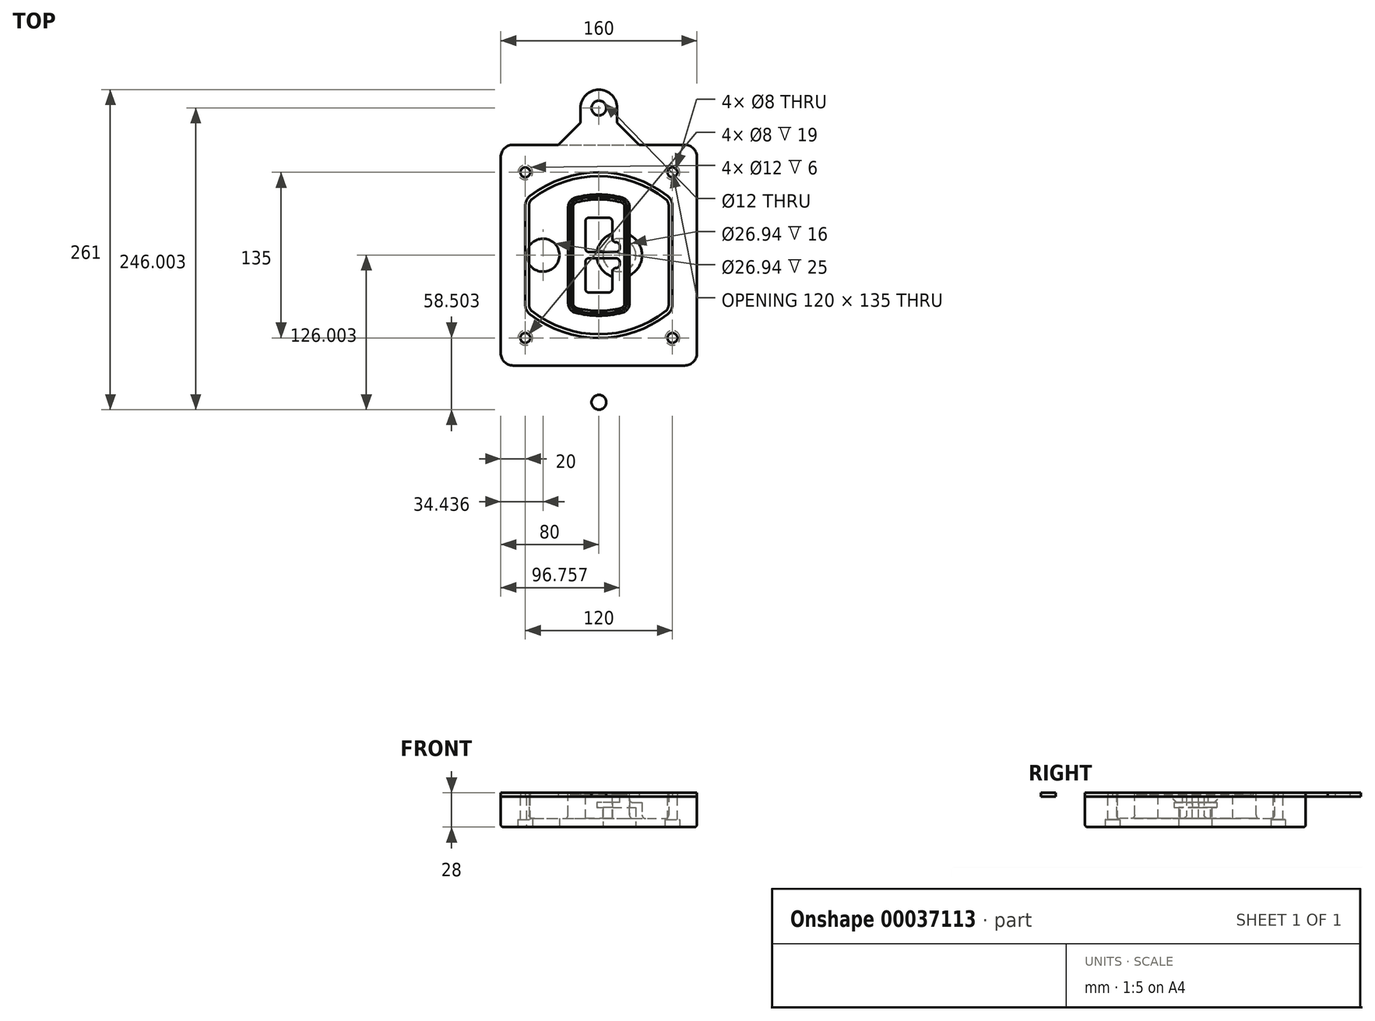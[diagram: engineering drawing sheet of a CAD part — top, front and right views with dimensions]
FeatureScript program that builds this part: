
annotation { "Feature Type Name" : "Feature", "Feature Type Description" : "" }
export const myFeature = defineFeature(function(context is Context, id is Id, definition is map)
    precondition{}
    {
        {
            var Q0;
            Q0=qCreatedBy(makeId("Top.planeOp"),FACE);
            var sketch = newSketch(context, id + "F0", { "sketchPlane" : qUnion([Q0])});
            skPoint(sketch, "E0.rect.middle", {"position": v(0, 0) * mm});
            skLineSegment(sketch, "E1.bottom", {"start": v(24.05, 28.38) * mm, "end": v(164.05, 28.38) * mm});
            skLineSegment(sketch, "E1.top", {"start": v(24.05, 208.38) * mm, "end": v(164.05, 208.38) * mm});
            skLineSegment(sketch, "E1.left", {"start": v(14.05, 38.38) * mm, "end": v(14.05, 198.38) * mm});
            skLineSegment(sketch, "E1.right", {"start": v(174.05, 38.38) * mm, "end": v(174.05, 198.38) * mm});
            skLineSegment(sketch, "E2", {"start": v(14.05, 208.38) * mm, "end": v(174.05, 28.38) * mm, "construction": true});
            skLineSegment(sketch, "E3", {"start": v(174.05, 208.38) * mm, "end": v(14.05, 28.38) * mm, "construction": true});
            skCircle(sketch, "E4", {"center": v(34.05, 185.88) * mm, "radius": 4 * mm});
            skCircle(sketch, "E5", {"center": v(154.05, 185.88) * mm, "radius": 4 * mm});
            skCircle(sketch, "E6", {"center": v(154.05, 50.88) * mm, "radius": 4 * mm});
            skCircle(sketch, "E7", {"center": v(34.05, 50.88) * mm, "radius": 4 * mm});
            skLineSegment(sketch, "E8", {"start": v(34.05, 185.88) * mm, "end": v(154.05, 185.88) * mm, "construction": true});
            skLineSegment(sketch, "E9", {"start": v(154.05, 185.88) * mm, "end": v(154.05, 50.88) * mm, "construction": true});
            skLineSegment(sketch, "E10", {"start": v(154.05, 50.88) * mm, "end": v(34.05, 50.88) * mm, "construction": true});
            skLineSegment(sketch, "E11", {"start": v(34.05, 50.88) * mm, "end": v(34.05, 185.88) * mm, "construction": true});
            skLineSegment(sketch, "E12", {"start": v(34.05, 158.68) * mm, "end": v(34.05, 78.09) * mm});
            skLineSegment(sketch, "E13", {"start": v(154.05, 158.68) * mm, "end": v(154.05, 78.09) * mm});
            skArc(sketch, "E14", {"start": v(150.2, 166.56) * mm, "mid": v(94.05, 185.88) * mm, "end": v(37.9, 166.56) * mm});
            skArc(sketch, "E15", {"start": v(37.9, 70.2) * mm, "mid": v(94.05, 50.88) * mm, "end": v(150.2, 70.2) * mm});
            skLineSegment(sketch, "E16", {"start": v(34.05, 118.38) * mm, "end": v(154.05, 118.38) * mm, "construction": true});
            skPoint(sketch, "E17.visualSharp", {"position": v(34.05, 73.38) * mm});
            skArc(sketch, "E17.filletArc", {"start": v(34.05, 78.09) * mm, "mid": v(35.06, 73.7) * mm, "end": v(37.9, 70.2) * mm});
            skPoint(sketch, "E18.visualSharp", {"position": v(34.05, 163.38) * mm});
            skArc(sketch, "E18.filletArc", {"start": v(37.9, 166.56) * mm, "mid": v(35.06, 163.06) * mm, "end": v(34.05, 158.68) * mm});
            skPoint(sketch, "E19.visualSharp", {"position": v(154.05, 163.38) * mm});
            skArc(sketch, "E19.filletArc", {"start": v(154.05, 158.68) * mm, "mid": v(153.04, 163.06) * mm, "end": v(150.2, 166.56) * mm});
            skPoint(sketch, "E20.visualSharp", {"position": v(154.05, 73.38) * mm});
            skArc(sketch, "E20.filletArc", {"start": v(150.2, 70.2) * mm, "mid": v(153.04, 73.7) * mm, "end": v(154.05, 78.09) * mm});
            skPoint(sketch, "E21.visualSharp", {"position": v(14.05, 208.38) * mm});
            skArc(sketch, "E21.filletArc", {"start": v(24.05, 208.38) * mm, "mid": v(16.98, 205.45) * mm, "end": v(14.05, 198.38) * mm});
            skPoint(sketch, "E22.visualSharp", {"position": v(174.05, 208.38) * mm});
            skArc(sketch, "E22.filletArc", {"start": v(174.05, 198.38) * mm, "mid": v(171.12, 205.45) * mm, "end": v(164.05, 208.38) * mm});
            skPoint(sketch, "E23.visualSharp", {"position": v(174.05, 28.38) * mm});
            skArc(sketch, "E23.filletArc", {"start": v(164.05, 28.38) * mm, "mid": v(171.12, 31.31) * mm, "end": v(174.05, 38.38) * mm});
            skPoint(sketch, "E24.visualSharp", {"position": v(14.05, 28.38) * mm});
            skArc(sketch, "E24.filletArc", {"start": v(14.05, 38.38) * mm, "mid": v(16.98, 31.31) * mm, "end": v(24.05, 28.38) * mm});
            skArc(sketch, "E25.0", {"start": v(151.05, 158.68) * mm, "mid": v(150.34, 161.75) * mm, "end": v(148.36, 164.2) * mm});
            skLineSegment(sketch, "E25.1", {"start": v(151.05, 158.68) * mm, "end": v(151.05, 78.09) * mm});
            skArc(sketch, "E25.2", {"start": v(148.36, 72.57) * mm, "mid": v(150.34, 75.02) * mm, "end": v(151.05, 78.09) * mm});
            skArc(sketch, "E25.3", {"start": v(39.74, 72.57) * mm, "mid": v(94.05, 53.88) * mm, "end": v(148.36, 72.57) * mm});
            skArc(sketch, "E25.4", {"start": v(37.05, 78.09) * mm, "mid": v(37.76, 75.02) * mm, "end": v(39.74, 72.57) * mm});
            skArc(sketch, "E25.5", {"start": v(148.36, 164.2) * mm, "mid": v(94.05, 182.88) * mm, "end": v(39.74, 164.2) * mm});
            skLineSegment(sketch, "E25.6", {"start": v(37.05, 158.68) * mm, "end": v(37.05, 78.09) * mm});
            skArc(sketch, "E25.7", {"start": v(39.74, 164.2) * mm, "mid": v(37.76, 161.75) * mm, "end": v(37.05, 158.68) * mm});
            skArc(sketch, "E26.0", {"start": v(35.43, 169.71) * mm, "mid": v(31.47, 164.82) * mm, "end": v(30.05, 158.68) * mm});
            skArc(sketch, "E26.1", {"start": v(152.67, 169.71) * mm, "mid": v(94.05, 189.88) * mm, "end": v(35.43, 169.71) * mm});
            skArc(sketch, "E26.2", {"start": v(158.05, 158.68) * mm, "mid": v(156.63, 164.82) * mm, "end": v(152.67, 169.71) * mm});
            skLineSegment(sketch, "E26.3", {"start": v(158.05, 158.68) * mm, "end": v(158.05, 78.09) * mm});
            skArc(sketch, "E26.4", {"start": v(152.67, 67.05) * mm, "mid": v(156.63, 71.95) * mm, "end": v(158.05, 78.09) * mm});
            skLineSegment(sketch, "E26.5", {"start": v(30.05, 158.68) * mm, "end": v(30.05, 78.09) * mm});
            skArc(sketch, "E26.6", {"start": v(35.43, 67.05) * mm, "mid": v(94.05, 46.88) * mm, "end": v(152.67, 67.05) * mm});
            skArc(sketch, "E26.7", {"start": v(30.05, 78.09) * mm, "mid": v(31.47, 71.95) * mm, "end": v(35.43, 67.05) * mm});
            skSolve(sketch);
        }
        {
            var Q0;
            Q0=makeQuery(id+"F0.imprint","IMPRINT",FACE,{"disambiguationData":[TD([[makeQuery(id+"F0.imprint","IMPRINT",EDGE,{"derivedFrom":sQuery(id+"F0.wireOp",EDGE,"E1.bottom")}),1.0]])]});
            var Q1;
            Q1=makeQuery(id+"F0.imprint","IMPRINT",FACE,{"disambiguationData":[TD([[makeQuery(id+"F0.imprint","IMPRINT",EDGE,{"derivedFrom":sQuery(id+"F0.wireOp",EDGE,"E12")}),1.0]])]});
            var Q2;
            Q2=makeQuery(id+"F0.imprint","IMPRINT",FACE,{"disambiguationData":[TD([[makeQuery(id+"F0.imprint","IMPRINT",EDGE,{"derivedFrom":sQuery(id+"F0.wireOp",EDGE,"E25.0")}),1.0]])]});
            var Q3;
            Q3=makeQuery(id+"F0.imprint","IMPRINT",FACE,{"disambiguationData":[TD([[makeQuery(id+"F0.imprint","IMPRINT",EDGE,{"derivedFrom":sQuery(id+"F0.wireOp",EDGE,"E12")}),-1.0]])]});
            extrude(context, id + "F1", {"entities" : qUnion([Q0, Q1, Q2, Q3]), "oppositeDirection" : true, "depth" : 25 * mm});
        }
        {
            var Q0;
            Q0=makeQuery(id+"F0.imprint","IMPRINT",FACE,{"disambiguationData":[TD([[makeQuery(id+"F0.imprint","IMPRINT",EDGE,{"derivedFrom":sQuery(id+"F0.wireOp",EDGE,"E12")}),1.0]])]});
            extrude(context, id + "F2", {"entities" : qUnion([Q0]), "operationType" : NewBodyOperationType.ADD, "depth" : 3 * mm});
        }
        {
            var Q0;
            Q0=makeQuery(id+"F0.imprint","IMPRINT",FACE,{"disambiguationData":[TD([[makeQuery(id+"F0.imprint","IMPRINT",EDGE,{"derivedFrom":sQuery(id+"F0.wireOp",EDGE,"E25.0")}),1.0]])]});
            extrude(context, id + "F3", {"entities" : qUnion([Q0]), "operationType" : NewBodyOperationType.REMOVE, "oppositeDirection" : true, "depth" : 18 * mm});
        }
        {
            var Q0;
            Q0=makeQuery(id+"F2.opExtrude","CAP_FACE",FACE,{"disambiguationData":[OSD([sQuery(id+"F0.wireOp",EDGE,"E12"),sQuery(id+"F0.wireOp",EDGE,"E13"),sQuery(id+"F0.wireOp",EDGE,"E14"),sQuery(id+"F0.wireOp",EDGE,"E15"),sQuery(id+"F0.wireOp",EDGE,"E17.filletArc"),sQuery(id+"F0.wireOp",EDGE,"E18.filletArc"),sQuery(id+"F0.wireOp",EDGE,"E19.filletArc"),sQuery(id+"F0.wireOp",EDGE,"E20.filletArc"),sQuery(id+"F0.wireOp",EDGE,"E25.0"),sQuery(id+"F0.wireOp",EDGE,"E25.1"),sQuery(id+"F0.wireOp",EDGE,"E25.2"),sQuery(id+"F0.wireOp",EDGE,"E25.3"),sQuery(id+"F0.wireOp",EDGE,"E25.4"),sQuery(id+"F0.wireOp",EDGE,"E25.5"),sQuery(id+"F0.wireOp",EDGE,"E25.6"),sQuery(id+"F0.wireOp",EDGE,"E25.7")])],"isStart":false});
            var sketch = newSketch(context, id + "F4", { "sketchPlane" : qUnion([Q0])});
            skArc(sketch, "E27.0", {"start": v(74.97, 71.41) * mm, "mid": v(94.05, 68.88) * mm, "end": v(113.13, 71.41) * mm});
            skArc(sketch, "E28.0", {"start": v(113.13, 165.35) * mm, "mid": v(94.05, 167.88) * mm, "end": v(74.97, 165.35) * mm});
            skLineSegment(sketch, "E29", {"start": v(69.05, 157.63) * mm, "end": v(69.05, 79.14) * mm});
            skLineSegment(sketch, "E30", {"start": v(119.05, 157.63) * mm, "end": v(119.05, 79.14) * mm});
            skLineSegment(sketch, "E31", {"start": v(69.05, 163.48) * mm, "end": v(119.05, 163.48) * mm, "construction": true});
            skLineSegment(sketch, "E32", {"start": v(69.05, 73.28) * mm, "end": v(119.05, 73.28) * mm, "construction": true});
            skPoint(sketch, "E33.visualSharp", {"position": v(69.05, 163.48) * mm});
            skArc(sketch, "E33.filletArc", {"start": v(74.97, 165.35) * mm, "mid": v(70.7, 162.5) * mm, "end": v(69.05, 157.63) * mm});
            skPoint(sketch, "E34.visualSharp", {"position": v(119.05, 163.48) * mm});
            skArc(sketch, "E34.filletArc", {"start": v(119.05, 157.63) * mm, "mid": v(117.4, 162.5) * mm, "end": v(113.13, 165.35) * mm});
            skPoint(sketch, "E35.visualSharp", {"position": v(119.05, 73.28) * mm});
            skArc(sketch, "E35.filletArc", {"start": v(113.13, 71.41) * mm, "mid": v(117.4, 74.27) * mm, "end": v(119.05, 79.14) * mm});
            skPoint(sketch, "E36.visualSharp", {"position": v(69.05, 73.28) * mm});
            skArc(sketch, "E36.filletArc", {"start": v(69.05, 79.14) * mm, "mid": v(70.7, 74.27) * mm, "end": v(74.97, 71.41) * mm});
            skArc(sketch, "E37.0", {"start": v(148.36, 164.2) * mm, "mid": v(94.05, 182.88) * mm, "end": v(39.74, 164.2) * mm});
            skArc(sketch, "E37.1", {"start": v(39.74, 164.2) * mm, "mid": v(37.76, 161.75) * mm, "end": v(37.05, 158.68) * mm});
            skLineSegment(sketch, "E37.2", {"start": v(37.05, 158.68) * mm, "end": v(37.05, 78.09) * mm});
            skArc(sketch, "E37.3", {"start": v(37.05, 78.09) * mm, "mid": v(37.76, 75.02) * mm, "end": v(39.74, 72.57) * mm});
            skArc(sketch, "E37.4", {"start": v(39.74, 72.57) * mm, "mid": v(94.05, 53.88) * mm, "end": v(148.36, 72.57) * mm});
            skArc(sketch, "E37.5", {"start": v(148.36, 72.57) * mm, "mid": v(150.34, 75.02) * mm, "end": v(151.05, 78.09) * mm});
            skLineSegment(sketch, "E37.6", {"start": v(151.05, 158.68) * mm, "end": v(151.05, 78.09) * mm});
            skArc(sketch, "E37.7", {"start": v(151.05, 158.68) * mm, "mid": v(150.34, 161.75) * mm, "end": v(148.36, 164.2) * mm});
            skLineSegment(sketch, "E38.0", {"start": v(117.05, 157.63) * mm, "end": v(117.05, 79.14) * mm});
            skArc(sketch, "E38.1", {"start": v(112.61, 73.34) * mm, "mid": v(115.81, 75.49) * mm, "end": v(117.05, 79.14) * mm});
            skArc(sketch, "E38.2", {"start": v(75.49, 73.34) * mm, "mid": v(94.05, 70.88) * mm, "end": v(112.61, 73.34) * mm});
            skArc(sketch, "E38.3", {"start": v(71.05, 79.14) * mm, "mid": v(72.29, 75.49) * mm, "end": v(75.49, 73.34) * mm});
            skLineSegment(sketch, "E38.4", {"start": v(71.05, 157.63) * mm, "end": v(71.05, 79.14) * mm});
            skArc(sketch, "E38.5", {"start": v(117.05, 157.63) * mm, "mid": v(115.81, 161.28) * mm, "end": v(112.61, 163.42) * mm});
            skArc(sketch, "E38.6", {"start": v(75.49, 163.42) * mm, "mid": v(72.29, 161.28) * mm, "end": v(71.05, 157.63) * mm});
            skArc(sketch, "E38.7", {"start": v(112.61, 163.42) * mm, "mid": v(94.05, 165.88) * mm, "end": v(75.49, 163.42) * mm});
            skArc(sketch, "E39.0", {"start": v(115.05, 157.63) * mm, "mid": v(114.23, 160.06) * mm, "end": v(112.1, 161.5) * mm});
            skLineSegment(sketch, "E39.1", {"start": v(115.05, 157.63) * mm, "end": v(115.05, 79.14) * mm});
            skArc(sketch, "E39.2", {"start": v(112.1, 75.27) * mm, "mid": v(114.23, 76.7) * mm, "end": v(115.05, 79.14) * mm});
            skArc(sketch, "E39.3", {"start": v(76, 75.27) * mm, "mid": v(94.05, 72.88) * mm, "end": v(112.1, 75.27) * mm});
            skArc(sketch, "E39.4", {"start": v(73.05, 79.14) * mm, "mid": v(73.87, 76.7) * mm, "end": v(76, 75.27) * mm});
            skArc(sketch, "E39.5", {"start": v(112.1, 161.5) * mm, "mid": v(94.05, 163.88) * mm, "end": v(76, 161.5) * mm});
            skLineSegment(sketch, "E39.6", {"start": v(73.05, 157.63) * mm, "end": v(73.05, 79.14) * mm});
            skArc(sketch, "E39.7", {"start": v(76, 161.5) * mm, "mid": v(73.87, 160.06) * mm, "end": v(73.05, 157.63) * mm});
            skLineSegment(sketch, "E40", {"start": v(69.05, 118.38) * mm, "end": v(119.05, 118.38) * mm, "construction": true});
            skLineSegment(sketch, "E41", {"start": v(83.05, 123.88) * mm, "end": v(83.05, 145.88) * mm});
            skLineSegment(sketch, "E42", {"start": v(86.05, 148.88) * mm, "end": v(102.05, 148.88) * mm});
            skLineSegment(sketch, "E43", {"start": v(105.05, 145.88) * mm, "end": v(105.05, 131.88) * mm});
            skLineSegment(sketch, "E44", {"start": v(108.05, 128.88) * mm, "end": v(108.05, 128.88) * mm});
            skLineSegment(sketch, "E45", {"start": v(111.05, 125.88) * mm, "end": v(111.05, 123.88) * mm});
            skLineSegment(sketch, "E46", {"start": v(108.05, 120.88) * mm, "end": v(86.05, 120.88) * mm});
            skPoint(sketch, "E47.visualSharp", {"position": v(83.05, 148.88) * mm});
            skArc(sketch, "E47.filletArc", {"start": v(86.05, 148.88) * mm, "mid": v(83.93, 148) * mm, "end": v(83.05, 145.88) * mm});
            skPoint(sketch, "E48.visualSharp", {"position": v(105.05, 148.88) * mm});
            skArc(sketch, "E48.filletArc", {"start": v(105.05, 145.88) * mm, "mid": v(104.17, 148) * mm, "end": v(102.05, 148.88) * mm});
            skPoint(sketch, "E49.visualSharp", {"position": v(105.05, 128.88) * mm});
            skArc(sketch, "E49.filletArc", {"start": v(105.05, 131.88) * mm, "mid": v(105.93, 129.76) * mm, "end": v(108.05, 128.88) * mm});
            skPoint(sketch, "E50.visualSharp", {"position": v(111.05, 128.88) * mm});
            skArc(sketch, "E50.filletArc", {"start": v(111.05, 125.88) * mm, "mid": v(110.17, 128) * mm, "end": v(108.05, 128.88) * mm});
            skPoint(sketch, "E51.visualSharp", {"position": v(111.05, 120.88) * mm});
            skArc(sketch, "E51.filletArc", {"start": v(108.05, 120.88) * mm, "mid": v(110.17, 121.76) * mm, "end": v(111.05, 123.88) * mm});
            skPoint(sketch, "E52.visualSharp", {"position": v(83.05, 120.88) * mm});
            skArc(sketch, "E52.filletArc", {"start": v(83.05, 123.88) * mm, "mid": v(83.93, 121.76) * mm, "end": v(86.05, 120.88) * mm});
            skLineSegment(sketch, "E53.0.MirrorCS", {"start": v(108.05, 115.88) * mm, "end": v(86.05, 115.88) * mm});
            skArc(sketch, "E54.0.MirrorCS", {"start": v(83.05, 112.88) * mm, "mid": v(83.93, 115) * mm, "end": v(86.05, 115.88) * mm});
            skLineSegment(sketch, "E55.0.MirrorCS", {"start": v(83.05, 112.88) * mm, "end": v(83.05, 90.88) * mm});
            skArc(sketch, "E56.0.MirrorCS", {"start": v(86.05, 87.88) * mm, "mid": v(83.93, 88.76) * mm, "end": v(83.05, 90.88) * mm});
            skLineSegment(sketch, "E57.0.MirrorCS", {"start": v(86.05, 87.88) * mm, "end": v(102.05, 87.88) * mm});
            skArc(sketch, "E58.0.MirrorCS", {"start": v(105.05, 90.88) * mm, "mid": v(104.17, 88.76) * mm, "end": v(102.05, 87.88) * mm});
            skLineSegment(sketch, "E59.0.MirrorCS", {"start": v(105.05, 90.88) * mm, "end": v(105.05, 104.88) * mm});
            skArc(sketch, "E60.0.MirrorCS", {"start": v(105.05, 104.88) * mm, "mid": v(105.93, 107) * mm, "end": v(108.05, 107.88) * mm});
            skArc(sketch, "E61.0.MirrorCS", {"start": v(111.05, 110.88) * mm, "mid": v(110.17, 108.76) * mm, "end": v(108.05, 107.88) * mm});
            skLineSegment(sketch, "E62.0.MirrorCS", {"start": v(111.05, 110.88) * mm, "end": v(111.05, 112.88) * mm});
            skArc(sketch, "E63.0.MirrorCS", {"start": v(108.05, 115.88) * mm, "mid": v(110.17, 115) * mm, "end": v(111.05, 112.88) * mm});
            skSolve(sketch);
        }
        {
            var Q0;
            Q0=makeQuery(id+"F4.imprint","IMPRINT",FACE,{"disambiguationData":[TD([[makeQuery(id+"F4.imprint","IMPRINT",EDGE,{"derivedFrom":sQuery(id+"F4.wireOp",EDGE,"E27.0")}),1.0]])]});
            var Q1;
            Q1=makeQuery(id+"F4.imprint","IMPRINT",FACE,{"disambiguationData":[TD([[makeQuery(id+"F4.imprint","IMPRINT",EDGE,{"derivedFrom":sQuery(id+"F4.wireOp",EDGE,"E38.0")}),-1.0]])]});
            var Q2;
            Q2=makeQuery(id+"F4.imprint","IMPRINT",FACE,{"disambiguationData":[TD([[makeQuery(id+"F4.imprint","IMPRINT",EDGE,{"derivedFrom":sQuery(id+"F4.wireOp",EDGE,"E39.0")}),1.0]])]});
            extrude(context, id + "F5", {"entities" : qUnion([Q0, Q1, Q2]), "operationType" : NewBodyOperationType.ADD, "endBound" : BoundingType.UP_TO_NEXT, "oppositeDirection" : true, "depth" : 25 * mm});
        }
        {
            var Q0;
            Q0=makeQuery(id+"F4.imprint","IMPRINT",FACE,{"disambiguationData":[TD([[makeQuery(id+"F4.imprint","IMPRINT",EDGE,{"derivedFrom":sQuery(id+"F4.wireOp",EDGE,"E38.0")}),-1.0]])]});
            extrude(context, id + "F6", {"entities" : qUnion([Q0]), "operationType" : NewBodyOperationType.REMOVE, "oppositeDirection" : true, "depth" : 2 * mm});
        }
        {
            var Q0;
            Q0=makeQuery(id+"F1.opExtrude","CAP_FACE",FACE,{"disambiguationData":[OSD([sQuery(id+"F0.wireOp",EDGE,"E1.bottom"),sQuery(id+"F0.wireOp",EDGE,"E1.top"),sQuery(id+"F0.wireOp",EDGE,"E1.left"),sQuery(id+"F0.wireOp",EDGE,"E1.right"),sQuery(id+"F0.wireOp",EDGE,"E4"),sQuery(id+"F0.wireOp",EDGE,"E5"),sQuery(id+"F0.wireOp",EDGE,"E6"),sQuery(id+"F0.wireOp",EDGE,"E7"),sQuery(id+"F0.wireOp",EDGE,"E21.filletArc"),sQuery(id+"F0.wireOp",EDGE,"E22.filletArc"),sQuery(id+"F0.wireOp",EDGE,"E23.filletArc"),sQuery(id+"F0.wireOp",EDGE,"E24.filletArc")])],"isStart":false});
            var sketch = newSketch(context, id + "F7", { "sketchPlane" : qUnion([Q0])});
            skCircle(sketch, "E64", {"center": v(110.8, -118.38) * mm, "radius": 13.47 * mm});
            skCircle(sketch, "E65", {"center": v(48.49, -118.38) * mm, "radius": 13.47 * mm});
            skLineSegment(sketch, "E66", {"start": v(174.05, -118.38) * mm, "end": v(14.05, -118.38) * mm});
            skCircle(sketch, "E67", {"center": v(110.8, -118.38) * mm, "radius": 18.47 * mm});
            skCircle(sketch, "E68", {"center": v(154.05, -185.88) * mm, "radius": 6 * mm});
            skCircle(sketch, "E69", {"center": v(34.05, -185.88) * mm, "radius": 6 * mm});
            skCircle(sketch, "E70", {"center": v(34.05, -50.88) * mm, "radius": 6 * mm});
            skCircle(sketch, "E71", {"center": v(154.05, -50.88) * mm, "radius": 6 * mm});
            skSolve(sketch);
        }
        {
            var Q0;
            {var subQ1=sQuery(id+"F7.wireOp",EDGE,"E66");var subQ4=sQuery(id+"F7.wireOp",EDGE,"E64");var subQ6=makeQuery(id+"F7.imprint","INTERSECT",VERTEX,{"disambiguationData":[OD(0.0)],"derivedFrom":[subQ4,subQ1]});Q0=makeQuery(id+"F7.imprint","IMPRINT",FACE,{"disambiguationData":[TD([[makeQuery(id+"F7.imprint","IMPRINT",EDGE,{"disambiguationData":[TD([[subQ6,-1.0]])],"derivedFrom":subQ4}),-1.0]])]});}
            var Q1;
            {var subQ0=sQuery(id+"F7.wireOp",EDGE,"E66");var subQ1=sQuery(id+"F7.wireOp",EDGE,"E64");var subQ3=makeQuery(id+"F7.imprint","INTERSECT",VERTEX,{"disambiguationData":[OD(0.0)],"derivedFrom":[subQ1,subQ0]});Q1=makeQuery(id+"F7.imprint","IMPRINT",FACE,{"disambiguationData":[TD([[makeQuery(id+"F7.imprint","IMPRINT",EDGE,{"disambiguationData":[TD([[subQ3,-1.0]])],"derivedFrom":subQ1}),1.0]])]});}
            var Q2;
            {var subQ0=sQuery(id+"F7.wireOp",EDGE,"E66");var subQ1=sQuery(id+"F7.wireOp",EDGE,"E64");var subQ3=makeQuery(id+"F7.imprint","INTERSECT",VERTEX,{"disambiguationData":[OD(0.0)],"derivedFrom":[subQ1,subQ0]});Q2=makeQuery(id+"F7.imprint","IMPRINT",FACE,{"disambiguationData":[TD([[makeQuery(id+"F7.imprint","IMPRINT",EDGE,{"disambiguationData":[TD([[subQ3,1.0]])],"derivedFrom":subQ1}),1.0]])]});}
            var Q3;
            {var subQ1=sQuery(id+"F7.wireOp",EDGE,"E66");var subQ4=sQuery(id+"F7.wireOp",EDGE,"E64");var subQ6=makeQuery(id+"F7.imprint","INTERSECT",VERTEX,{"disambiguationData":[OD(0.0)],"derivedFrom":[subQ4,subQ1]});Q3=makeQuery(id+"F7.imprint","IMPRINT",FACE,{"disambiguationData":[TD([[makeQuery(id+"F7.imprint","IMPRINT",EDGE,{"disambiguationData":[TD([[subQ6,1.0]])],"derivedFrom":subQ4}),-1.0]])]});}
            extrude(context, id + "F8", {"entities" : qUnion([Q0, Q1, Q2, Q3]), "operationType" : NewBodyOperationType.ADD, "oppositeDirection" : true, "depth" : 20 * mm});
        }
        {
            var Q0;
            {var subQ0=sQuery(id+"F7.wireOp",EDGE,"E66");var subQ1=sQuery(id+"F7.wireOp",EDGE,"E64");var subQ3=makeQuery(id+"F7.imprint","INTERSECT",VERTEX,{"disambiguationData":[OD(0.0)],"derivedFrom":[subQ1,subQ0]});Q0=makeQuery(id+"F7.imprint","IMPRINT",FACE,{"disambiguationData":[TD([[makeQuery(id+"F7.imprint","IMPRINT",EDGE,{"disambiguationData":[TD([[subQ3,-1.0]])],"derivedFrom":subQ1}),1.0]])]});}
            var Q1;
            {var subQ0=sQuery(id+"F7.wireOp",EDGE,"E66");var subQ1=sQuery(id+"F7.wireOp",EDGE,"E64");var subQ3=makeQuery(id+"F7.imprint","INTERSECT",VERTEX,{"disambiguationData":[OD(0.0)],"derivedFrom":[subQ1,subQ0]});Q1=makeQuery(id+"F7.imprint","IMPRINT",FACE,{"disambiguationData":[TD([[makeQuery(id+"F7.imprint","IMPRINT",EDGE,{"disambiguationData":[TD([[subQ3,1.0]])],"derivedFrom":subQ1}),1.0]])]});}
            extrude(context, id + "F9", {"entities" : qUnion([Q0, Q1]), "operationType" : NewBodyOperationType.REMOVE, "oppositeDirection" : true, "depth" : 16 * mm});
        }
        {
            var Q0;
            {var subQ0=sQuery(id+"F7.wireOp",EDGE,"E66");var subQ1=sQuery(id+"F7.wireOp",EDGE,"E65");var subQ3=makeQuery(id+"F7.imprint","INTERSECT",VERTEX,{"disambiguationData":[OD(0.0)],"derivedFrom":[subQ1,subQ0]});Q0=makeQuery(id+"F7.imprint","IMPRINT",FACE,{"disambiguationData":[TD([[makeQuery(id+"F7.imprint","IMPRINT",EDGE,{"disambiguationData":[TD([[subQ3,-1.0]])],"derivedFrom":subQ1}),1.0]])]});}
            var Q1;
            {var subQ0=sQuery(id+"F7.wireOp",EDGE,"E66");var subQ1=sQuery(id+"F7.wireOp",EDGE,"E65");var subQ3=makeQuery(id+"F7.imprint","INTERSECT",VERTEX,{"disambiguationData":[OD(0.0)],"derivedFrom":[subQ1,subQ0]});Q1=makeQuery(id+"F7.imprint","IMPRINT",FACE,{"disambiguationData":[TD([[makeQuery(id+"F7.imprint","IMPRINT",EDGE,{"disambiguationData":[TD([[subQ3,1.0]])],"derivedFrom":subQ1}),1.0]])]});}
            extrude(context, id + "F10", {"entities" : qUnion([Q0, Q1]), "operationType" : NewBodyOperationType.REMOVE, "oppositeDirection" : true, "depth" : 25 * mm});
        }
        {
            var Q0;
            Q0=makeQuery(id+"F7.imprint","IMPRINT",FACE,{"disambiguationData":[TD([[makeQuery(id+"F7.imprint","IMPRINT",EDGE,{"derivedFrom":sQuery(id+"F7.wireOp",EDGE,"E68")}),1.0]])]});
            var Q1;
            Q1=makeQuery(id+"F7.imprint","IMPRINT",FACE,{"disambiguationData":[TD([[makeQuery(id+"F7.imprint","IMPRINT",EDGE,{"derivedFrom":makeQuery(id+"F1.opExtrude","CAP_EDGE",EDGE,{"disambiguationData":[OSD([sQuery(id+"F0.wireOp",EDGE,"E5")])],"isStart":false})}),-1.0]])]});
            var Q2;
            Q2=makeQuery(id+"F7.imprint","IMPRINT",FACE,{"disambiguationData":[TD([[makeQuery(id+"F7.imprint","IMPRINT",EDGE,{"derivedFrom":sQuery(id+"F7.wireOp",EDGE,"E69")}),1.0]])]});
            var Q3;
            Q3=makeQuery(id+"F7.imprint","IMPRINT",FACE,{"disambiguationData":[TD([[makeQuery(id+"F7.imprint","IMPRINT",EDGE,{"derivedFrom":makeQuery(id+"F1.opExtrude","CAP_EDGE",EDGE,{"disambiguationData":[OSD([sQuery(id+"F0.wireOp",EDGE,"E4")])],"isStart":false})}),-1.0]])]});
            var Q4;
            Q4=makeQuery(id+"F7.imprint","IMPRINT",FACE,{"disambiguationData":[TD([[makeQuery(id+"F7.imprint","IMPRINT",EDGE,{"derivedFrom":sQuery(id+"F7.wireOp",EDGE,"E70")}),1.0]])]});
            var Q5;
            Q5=makeQuery(id+"F7.imprint","IMPRINT",FACE,{"disambiguationData":[TD([[makeQuery(id+"F7.imprint","IMPRINT",EDGE,{"derivedFrom":makeQuery(id+"F1.opExtrude","CAP_EDGE",EDGE,{"disambiguationData":[OSD([sQuery(id+"F0.wireOp",EDGE,"E7")])],"isStart":false})}),-1.0]])]});
            var Q6;
            Q6=makeQuery(id+"F7.imprint","IMPRINT",FACE,{"disambiguationData":[TD([[makeQuery(id+"F7.imprint","IMPRINT",EDGE,{"derivedFrom":sQuery(id+"F7.wireOp",EDGE,"E71")}),1.0]])]});
            var Q7;
            Q7=makeQuery(id+"F7.imprint","IMPRINT",FACE,{"disambiguationData":[TD([[makeQuery(id+"F7.imprint","IMPRINT",EDGE,{"derivedFrom":makeQuery(id+"F1.opExtrude","CAP_EDGE",EDGE,{"disambiguationData":[OSD([sQuery(id+"F0.wireOp",EDGE,"E6")])],"isStart":false})}),-1.0]])]});
            extrude(context, id + "F11", {"entities" : qUnion([Q0, Q1, Q2, Q3, Q4, Q5, Q6, Q7]), "operationType" : NewBodyOperationType.REMOVE, "oppositeDirection" : true, "depth" : 6 * mm});
        }
        {
            var Q0;
            Q0=makeQuery(id+"F9.boolean.opBoolean","COPY",FACE,{"derivedFrom":makeQuery(id+"F9.opExtrude","CAP_FACE",FACE,{"disambiguationData":[OSD([sQuery(id+"F7.wireOp",EDGE,"E64")])],"isStart":false})});
            var sketch = newSketch(context, id + "F12", { "sketchPlane" : qUnion([Q0])});
            skArc(sketch, "E72.0", {"start": v(105.05, -100.83) * mm, "mid": v(96.62, -106.56) * mm, "end": v(92.5, -115.88) * mm});
            skArc(sketch, "E72.1", {"start": v(92.5, -120.88) * mm, "mid": v(96.62, -130.2) * mm, "end": v(105.05, -135.93) * mm});
            skLineSegment(sketch, "E73", {"start": v(92.5, -120.88) * mm, "end": v(108.05, -120.88) * mm});
            skLineSegment(sketch, "E74.0", {"start": v(108.05, -115.88) * mm, "end": v(92.5, -115.88) * mm});
            skArc(sketch, "E74.1", {"start": v(108.05, -115.88) * mm, "mid": v(110.17, -115) * mm, "end": v(111.05, -112.88) * mm});
            skLineSegment(sketch, "E74.2", {"start": v(111.05, -110.88) * mm, "end": v(111.05, -112.88) * mm});
            skArc(sketch, "E74.3", {"start": v(111.05, -110.88) * mm, "mid": v(110.17, -108.76) * mm, "end": v(108.05, -107.88) * mm});
            skArc(sketch, "E74.4", {"start": v(105.05, -104.88) * mm, "mid": v(105.93, -107) * mm, "end": v(108.05, -107.88) * mm});
            skLineSegment(sketch, "E74.5", {"start": v(105.05, -100.83) * mm, "end": v(105.05, -104.88) * mm});
            skLineSegment(sketch, "E74.7", {"start": v(108.05, -120.88) * mm, "end": v(92.5, -120.88) * mm});
            skArc(sketch, "E74.8", {"start": v(108.05, -120.88) * mm, "mid": v(110.17, -121.76) * mm, "end": v(111.05, -123.88) * mm});
            skLineSegment(sketch, "E74.9", {"start": v(111.05, -125.88) * mm, "end": v(111.05, -123.88) * mm});
            skArc(sketch, "E74.10", {"start": v(111.05, -125.88) * mm, "mid": v(110.17, -128) * mm, "end": v(108.05, -128.88) * mm});
            skArc(sketch, "E74.11", {"start": v(105.05, -131.88) * mm, "mid": v(105.93, -129.76) * mm, "end": v(108.05, -128.88) * mm});
            skLineSegment(sketch, "E74.12", {"start": v(105.05, -135.93) * mm, "end": v(105.05, -131.88) * mm});
            skPoint(sketch, "E75.orphan", {"position": v(105.05, -145.88) * mm});
            skPoint(sketch, "E76.orphan", {"position": v(86.05, -120.88) * mm});
            skPoint(sketch, "E77.orphan", {"position": v(86.05, -115.88) * mm});
            skPoint(sketch, "E78.orphan", {"position": v(105.05, -90.88) * mm});
            skSolve(sketch);
        }
        {
            var Q0;
            {var subQ7=sQuery(id+"F12.wireOp",EDGE,"E72.0");var subQ14=sQuery(id+"F12.wireOp",EDGE,"E72.1");var subQ16=sQuery(id+"F12.wireOp",EDGE,"E74.1");var subQ18=sQuery(id+"F12.wireOp",EDGE,"E74.8");Q0=qUnion([makeQuery(id+"F12.imprint","IMPRINT",FACE,{"disambiguationData":[TD([[makeQuery(id+"F12.imprint","IMPRINT",EDGE,{"derivedFrom":subQ7}),1.0]])]}),makeQuery(id+"F12.imprint","IMPRINT",FACE,{"disambiguationData":[TD([[makeQuery(id+"F12.imprint","IMPRINT",EDGE,{"derivedFrom":subQ14}),1.0]])]}),makeQuery(id+"F12.imprint","IMPRINT",FACE,{"disambiguationData":[TD([[makeQuery(id+"F12.imprint","IMPRINT",EDGE,{"derivedFrom":subQ16}),1.0]])]}),makeQuery(id+"F12.imprint","IMPRINT",FACE,{"disambiguationData":[TD([[makeQuery(id+"F12.imprint","IMPRINT",EDGE,{"derivedFrom":subQ18}),-1.0]])]})]);}
            var Q1;
            Q1=makeQuery(id+"F5.boolean.opBoolean","SPLIT",FACE,{"disambiguationData":[TD([makeQuery(id+"F5.opExtrude","SWEPT_FACE",FACE,{"disambiguationData":[OSD([sQuery(id+"F4.wireOp",EDGE,"E41")])]})])],"derivedFrom":makeQuery(id+"F3.boolean.opBoolean","COPY",FACE,{"derivedFrom":makeQuery(id+"F3.opExtrude","CAP_FACE",FACE,{"disambiguationData":[OSD([sQuery(id+"F0.wireOp",EDGE,"E25.0"),sQuery(id+"F0.wireOp",EDGE,"E25.1"),sQuery(id+"F0.wireOp",EDGE,"E25.2"),sQuery(id+"F0.wireOp",EDGE,"E25.3"),sQuery(id+"F0.wireOp",EDGE,"E25.4"),sQuery(id+"F0.wireOp",EDGE,"E25.5"),sQuery(id+"F0.wireOp",EDGE,"E25.6"),sQuery(id+"F0.wireOp",EDGE,"E25.7")])],"isStart":false})})});
            extrude(context, id + "F13", {"entities" : qUnion([Q0]), "operationType" : NewBodyOperationType.REMOVE, "endBound" : BoundingType.UP_TO_SURFACE, "endBoundEntityFace" : qUnion([Q1]), "depth" : 25 * mm});
        }
        {
            var Q0;
            Q0=makeQuery(id+"F3.boolean.opBoolean","COPY",EDGE,{"derivedFrom":makeQuery(id+"F3.opExtrude","CAP_EDGE",EDGE,{"disambiguationData":[OSD([sQuery(id+"F0.wireOp",EDGE,"E25.6")])],"isStart":false})});
            var Q1;
            Q1=makeQuery(id+"F8.boolean.opBoolean","INTERSECT",EDGE,{"derivedFrom":[makeQuery(id+"F5.opExtrude","SWEPT_FACE",FACE,{"disambiguationData":[OSD([sQuery(id+"F4.wireOp",EDGE,"E30")])]}),makeQuery(id+"F8.opExtrude","CAP_FACE",FACE,{"disambiguationData":[OSD([sQuery(id+"F7.wireOp",EDGE,"E67")])],"isStart":false})]});
            var Q2;
            Q2=makeQuery(id+"F8.boolean.opBoolean","INTERSECT",EDGE,{"disambiguationData":[OD(1.0)],"derivedFrom":[makeQuery(id+"F5.opExtrude","SWEPT_FACE",FACE,{"disambiguationData":[OSD([sQuery(id+"F4.wireOp",EDGE,"E30")])]}),makeQuery(id+"F8.opExtrude","SWEPT_FACE",FACE,{"disambiguationData":[OSD([sQuery(id+"F7.wireOp",EDGE,"E67")])]})]});
            var Q3;
            {var subQ0=sQuery(id+"F4.wireOp",EDGE,"E30");Q3=makeQuery(id+"F8.boolean.opBoolean","SPLIT",EDGE,{"disambiguationData":[TD([makeQuery(id+"F5.opExtrude","SWEPT_FACE",FACE,{"disambiguationData":[OSD([sQuery(id+"F4.wireOp",EDGE,"E35.filletArc")])]})])],"derivedFrom":makeQuery(id+"F5.opExtrude","CAP_EDGE",EDGE,{"disambiguationData":[OSD([subQ0])],"isStart":false})});}
            var Q4;
            {var subQ0=sQuery(id+"F0.wireOp",EDGE,"E25.7");var subQ1=sQuery(id+"F0.wireOp",EDGE,"E25.1");var subQ2=sQuery(id+"F0.wireOp",EDGE,"E25.6");var subQ3=sQuery(id+"F0.wireOp",EDGE,"E25.5");var subQ4=sQuery(id+"F0.wireOp",EDGE,"E25.4");var subQ5=sQuery(id+"F0.wireOp",EDGE,"E25.0");var subQ6=sQuery(id+"F0.wireOp",EDGE,"E25.2");var subQ7=sQuery(id+"F0.wireOp",EDGE,"E25.3");Q4=makeQuery(id+"F8.boolean.opBoolean","INTERSECT",EDGE,{"derivedFrom":[makeQuery(id+"F5.boolean.opBoolean","SPLIT",FACE,{"disambiguationData":[TD([makeQuery(id+"F2.opExtrude","SWEPT_FACE",FACE,{"disambiguationData":[OSD([subQ5])]})])],"derivedFrom":makeQuery(id+"F3.boolean.opBoolean","COPY",FACE,{"derivedFrom":makeQuery(id+"F3.opExtrude","CAP_FACE",FACE,{"disambiguationData":[OSD([subQ5,subQ1,subQ6,subQ7,subQ4,subQ3,subQ2,subQ0])],"isStart":false})})}),makeQuery(id+"F8.opExtrude","SWEPT_FACE",FACE,{"disambiguationData":[OSD([sQuery(id+"F7.wireOp",EDGE,"E67")])]})]});}
            var Q5;
            Q5=makeQuery(id+"F8.boolean.opBoolean","INTERSECT",EDGE,{"disambiguationData":[OD(0.0)],"derivedFrom":[makeQuery(id+"F5.opExtrude","SWEPT_FACE",FACE,{"disambiguationData":[OSD([sQuery(id+"F4.wireOp",EDGE,"E30")])]}),makeQuery(id+"F8.opExtrude","SWEPT_FACE",FACE,{"disambiguationData":[OSD([sQuery(id+"F7.wireOp",EDGE,"E67")])]})]});
            fillet(context, id + "F14", {"entities" : qUnion([Q0, Q1, Q2, Q3, Q4, Q5]), "radius" : 3 * mm, "tangentPropagation" : true, "allowEdgeOverflow" : false});
        }
        {
            var Q0;
            Q0=makeQuery(id+"F1.opExtrude","CAP_EDGE",EDGE,{"disambiguationData":[OSD([sQuery(id+"F0.wireOp",EDGE,"E1.bottom")])],"isStart":false});
            fillet(context, id + "F15", {"entities" : qUnion([Q0]), "radius" : 2 * mm, "tangentPropagation" : true, "allowEdgeOverflow" : false});
        }
        {
            var Q0;
            {var subQ0=sQuery(id+"F0.wireOp",EDGE,"E1.bottom");var subQ1=sQuery(id+"F0.wireOp",EDGE,"E1.top");var subQ2=sQuery(id+"F0.wireOp",EDGE,"E1.left");var subQ3=sQuery(id+"F0.wireOp",EDGE,"E1.right");var subQ4=sQuery(id+"F0.wireOp",EDGE,"E4");var subQ5=sQuery(id+"F0.wireOp",EDGE,"E5");var subQ6=sQuery(id+"F0.wireOp",EDGE,"E6");var subQ7=sQuery(id+"F0.wireOp",EDGE,"E7");var subQ8=sQuery(id+"F0.wireOp",EDGE,"E21.filletArc");var subQ9=sQuery(id+"F0.wireOp",EDGE,"E22.filletArc");var subQ10=sQuery(id+"F0.wireOp",EDGE,"E23.filletArc");var subQ11=sQuery(id+"F0.wireOp",EDGE,"E24.filletArc");Q0=makeQuery(id+"F2.boolean.opBoolean","SPLIT",FACE,{"disambiguationData":[TD([makeQuery(id+"F1.opExtrude","SWEPT_FACE",FACE,{"disambiguationData":[OSD([subQ0])]})])],"derivedFrom":makeQuery(id+"F1.opExtrude","CAP_FACE",FACE,{"disambiguationData":[OSD([subQ0,subQ1,subQ2,subQ3,subQ4,subQ5,subQ6,subQ7,subQ8,subQ9,subQ10,subQ11])],"isStart":true})});}
            var sketch = newSketch(context, id + "F16", { "sketchPlane" : qUnion([Q0])});
            skLineSegment(sketch, "E79", {"start": v(61.05, 208.38) * mm, "end": v(79.05, 226.38) * mm});
            skLineSegment(sketch, "E80", {"start": v(79.05, 226.38) * mm, "end": v(79.05, 238.38) * mm});
            skLineSegment(sketch, "E81", {"start": v(127.05, 208.38) * mm, "end": v(109.05, 226.38) * mm});
            skLineSegment(sketch, "E82", {"start": v(109.05, 226.38) * mm, "end": v(109.05, 238.38) * mm});
            skArc(sketch, "E83", {"start": v(109.05, 238.38) * mm, "mid": v(94.05, 253.38) * mm, "end": v(79.05, 238.38) * mm});
            skCircle(sketch, "E84", {"center": v(94.05, 238.38) * mm, "radius": 6 * mm});
            skLineSegment(sketch, "E85", {"start": v(94.05, 208.38) * mm, "end": v(94.05, 238.38) * mm, "construction": true});
            skLineSegment(sketch, "E86", {"start": v(79.05, 238.38) * mm, "end": v(109.05, 238.38) * mm, "construction": true});
            skLineSegment(sketch, "E87", {"start": v(14.05, 118.38) * mm, "end": v(174.05, 118.38) * mm, "construction": true});
            skLineSegment(sketch, "E88.MirrorCS", {"start": v(94.05, 28.38) * mm, "end": v(94.05, -1.62) * mm, "construction": true});
            skCircle(sketch, "E89.MirrorC", {"center": v(94.05, -1.62) * mm, "radius": 6 * mm});
            skArc(sketch, "E90.MirrorCS", {"start": v(109.05, -1.62) * mm, "mid": v(94.05, -16.62) * mm, "end": v(79.05, -1.62) * mm});
            skLineSegment(sketch, "E91.MirrorCS", {"start": v(109.05, 10.38) * mm, "end": v(109.05, -1.62) * mm});
            skLineSegment(sketch, "E92.MirrorCS", {"start": v(79.05, 10.38) * mm, "end": v(79.05, -1.62) * mm});
            skLineSegment(sketch, "E93.MirrorCS", {"start": v(61.05, 28.38) * mm, "end": v(79.05, 10.38) * mm});
            skLineSegment(sketch, "E94.MirrorCS", {"start": v(79.05, -1.62) * mm, "end": v(109.05, -1.62) * mm, "construction": true});
            skLineSegment(sketch, "E95.MirrorCS", {"start": v(127.05, 28.38) * mm, "end": v(109.05, 10.38) * mm});
            skLineSegment(sketch, "E96", {"start": v(127.05, 208.38) * mm, "end": v(61.05, 208.38) * mm, "construction": true});
            skLineSegment(sketch, "E97", {"start": v(127.05, 28.38) * mm, "end": v(61.05, 28.38) * mm, "construction": true});
            skSolve(sketch);
        }
        {
            var Q0;
            Q0=makeQuery(id+"F16.imprint","IMPRINT",FACE,{"disambiguationData":[TD([[makeQuery(id+"F16.imprint","IMPRINT",EDGE,{"derivedFrom":sQuery(id+"F16.wireOp",EDGE,"E89.MirrorC")}),1.0]])]});
            var Q1;
            {var subQ2=sQuery(id+"F16.wireOp",EDGE,"E79");Q1=makeQuery(id+"F16.imprint","IMPRINT",FACE,{"disambiguationData":[TD([[makeQuery(id+"F16.imprint","IMPRINT",EDGE,{"derivedFrom":subQ2}),-1.0]])]});}
            var Q2;
            Q2=makeQuery(id+"F16.imprint","IMPRINT",FACE,{"disambiguationData":[TD([[makeQuery(id+"F16.imprint","IMPRINT",EDGE,{"derivedFrom":makeQuery(id+"F1.opExtrude","CAP_EDGE",EDGE,{"disambiguationData":[OSD([sQuery(id+"F0.wireOp",EDGE,"E1.left")])],"isStart":true})}),-1.0]])]});
            var Q3;
            Q3=makeQuery(id+"F2.opExtrude","CAP_FACE",FACE,{"disambiguationData":[OSD([sQuery(id+"F0.wireOp",EDGE,"E12"),sQuery(id+"F0.wireOp",EDGE,"E13"),sQuery(id+"F0.wireOp",EDGE,"E14"),sQuery(id+"F0.wireOp",EDGE,"E15"),sQuery(id+"F0.wireOp",EDGE,"E17.filletArc"),sQuery(id+"F0.wireOp",EDGE,"E18.filletArc"),sQuery(id+"F0.wireOp",EDGE,"E19.filletArc"),sQuery(id+"F0.wireOp",EDGE,"E20.filletArc"),sQuery(id+"F0.wireOp",EDGE,"E25.0"),sQuery(id+"F0.wireOp",EDGE,"E25.1"),sQuery(id+"F0.wireOp",EDGE,"E25.2"),sQuery(id+"F0.wireOp",EDGE,"E25.3"),sQuery(id+"F0.wireOp",EDGE,"E25.4"),sQuery(id+"F0.wireOp",EDGE,"E25.5"),sQuery(id+"F0.wireOp",EDGE,"E25.6"),sQuery(id+"F0.wireOp",EDGE,"E25.7")])],"isStart":false});
            extrude(context, id + "F17", {"entities" : qUnion([Q0, Q1, Q2]), "endBound" : BoundingType.UP_TO_SURFACE, "endBoundEntityFace" : qUnion([Q3]), "depth" : 25 * mm});
        }
    });
